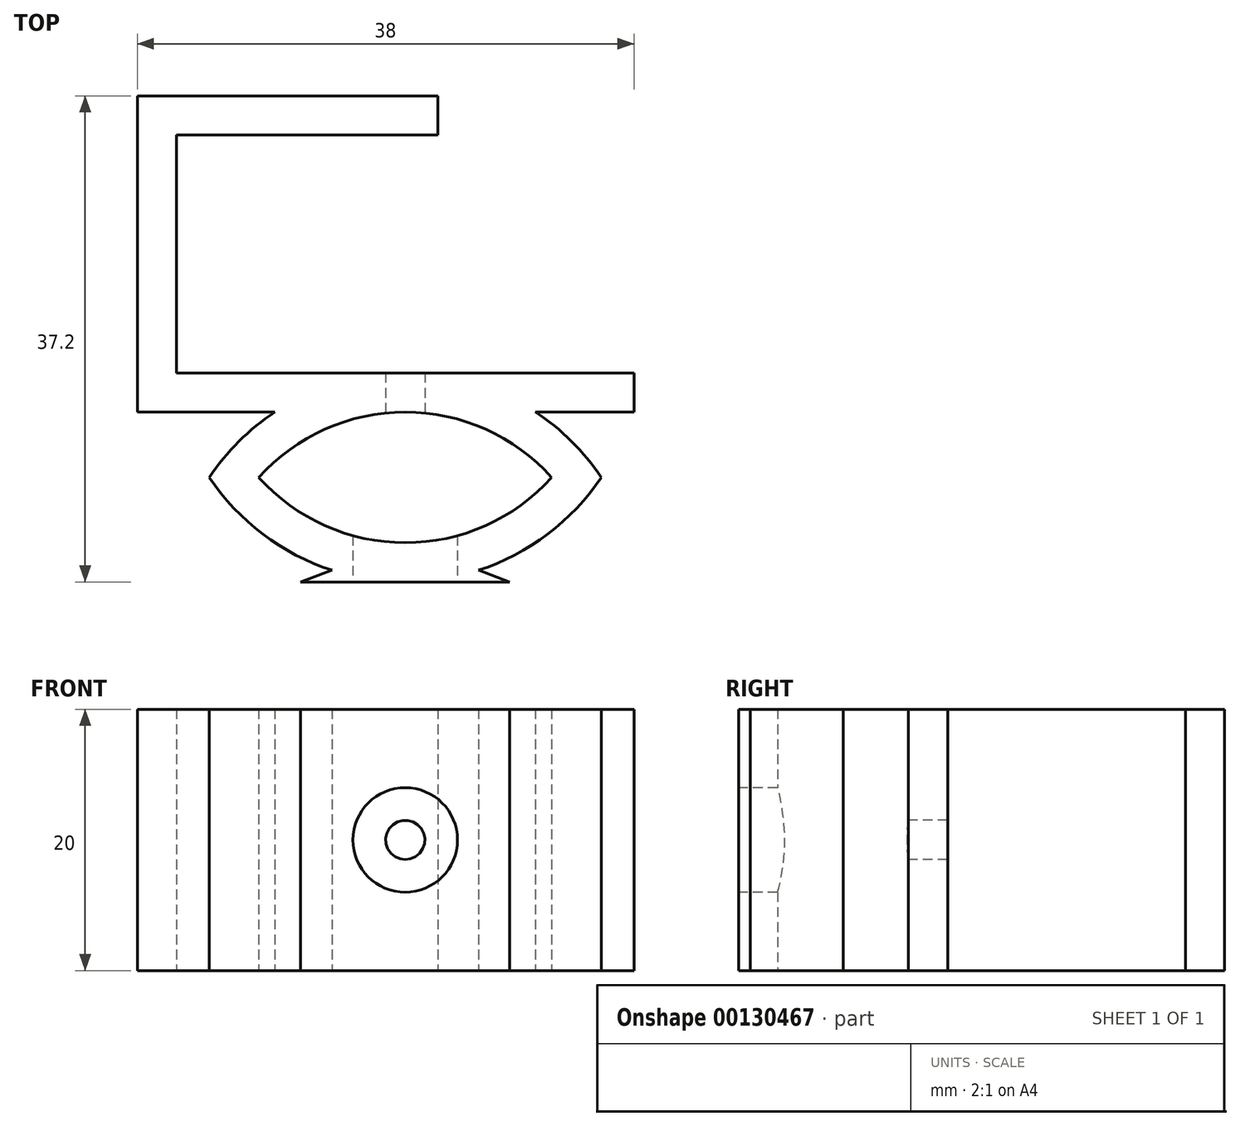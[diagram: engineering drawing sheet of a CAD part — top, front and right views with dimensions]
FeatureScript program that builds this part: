
annotation { "Feature Type Name" : "Feature", "Feature Type Description" : "" }
export const myFeature = defineFeature(function(context is Context, id is Id, definition is map)
    precondition{}
    {
        {
            var Q0;
            Q0=qCreatedBy(makeId("Top.planeOp"),FACE);
            var sketch = newSketch(context, id + "F0", { "sketchPlane" : qUnion([Q0])});
            skLineSegment(sketch, "E0", {"start": v(0, 0) * mm, "end": v(-20, 0) * mm});
            skLineSegment(sketch, "E1", {"start": v(-20, 0) * mm, "end": v(-20, -18.2) * mm});
            skLineSegment(sketch, "E2", {"start": v(-20, -18.2) * mm, "end": v(15, -18.2) * mm});
            skLineSegment(sketch, "E3.0", {"start": v(-23, -21.2) * mm, "end": v(15, -21.2) * mm});
            skLineSegment(sketch, "E3.1", {"start": v(-23, 3) * mm, "end": v(-23, -21.2) * mm});
            skLineSegment(sketch, "E3.2", {"start": v(0, 3) * mm, "end": v(-23, 3) * mm});
            skLineSegment(sketch, "E4", {"start": v(0, 3) * mm, "end": v(0, 0) * mm});
            skLineSegment(sketch, "E5", {"start": v(15, -18.2) * mm, "end": v(15, -21.2) * mm});
            skLineSegment(sketch, "E6", {"start": v(-17.5, -26.2) * mm, "end": v(12.5, -26.2) * mm, "construction": true});
            skLineSegment(sketch, "E7", {"start": v(-2.5, -18.2) * mm, "end": v(-2.5, -26.2) * mm, "construction": true});
            skPoint(sketch, "E8", {"position": v(-2.5, -26.2) * mm});
            skLineSegment(sketch, "E9", {"start": v(-2.5, -26.2) * mm, "end": v(-2.5, -34.2) * mm, "construction": true});
            skArc(sketch, "E10", {"start": v(12.5, -26.2) * mm, "mid": v(-2.5, -18.2) * mm, "end": v(-17.5, -26.2) * mm});
            skArc(sketch, "E11", {"start": v(-17.5, -26.2) * mm, "mid": v(-2.5, -34.2) * mm, "end": v(12.5, -26.2) * mm});
            skArc(sketch, "E12.0", {"start": v(8.7, -26.2) * mm, "mid": v(-2.5, -21.2) * mm, "end": v(-13.7, -26.2) * mm});
            skArc(sketch, "E12.1", {"start": v(-13.7, -26.2) * mm, "mid": v(-2.5, -31.2) * mm, "end": v(8.7, -26.2) * mm});
            skLineSegment(sketch, "E13", {"start": v(-2.5, -31.2) * mm, "end": v(-10.5, -34.2) * mm});
            skLineSegment(sketch, "E14", {"start": v(-10.5, -34.2) * mm, "end": v(5.5, -34.2) * mm});
            skLineSegment(sketch, "E15", {"start": v(5.5, -34.2) * mm, "end": v(-2.5, -31.2) * mm});
            skSolve(sketch);
        }
        {
            var Q0;
            Q0=makeQuery(id+"F0.imprint","IMPRINT",FACE,{"disambiguationData":[TD([[makeQuery(id+"F0.imprint","IMPRINT",EDGE,{"derivedFrom":sQuery(id+"F0.wireOp",EDGE,"E0")}),-1.0]])]});
            var Q1;
            {var subQ0=sQuery(id+"F0.wireOp",EDGE,"E10");var subQ1=sQuery(id+"F0.wireOp",EDGE,"E3.0");var subQ2=makeQuery(id+"F0.imprint","INTERSECT",VERTEX,{"disambiguationData":[OD(0.0)],"derivedFrom":[subQ1,subQ0]});Q1=makeQuery(id+"F0.imprint","IMPRINT",FACE,{"disambiguationData":[TD([[makeQuery(id+"F0.imprint","IMPRINT",EDGE,{"disambiguationData":[TD([[subQ2,-1.0]])],"derivedFrom":subQ1}),1.0]])]});}
            var Q2;
            {var subQ0=sQuery(id+"F0.wireOp",EDGE,"E5");Q2=makeQuery(id+"F0.imprint","IMPRINT",FACE,{"disambiguationData":[TD([[makeQuery(id+"F0.imprint","IMPRINT",EDGE,{"derivedFrom":subQ0}),-1.0]])]});}
            var Q3;
            {var subQ1=sQuery(id+"F0.wireOp",EDGE,"E10");var subQ3=sQuery(id+"F0.wireOp",EDGE,"E3.0");var subQ4=makeQuery(id+"F0.imprint","INTERSECT",VERTEX,{"disambiguationData":[OD(1.0)],"derivedFrom":[subQ3,subQ1]});Q3=makeQuery(id+"F0.imprint","IMPRINT",FACE,{"disambiguationData":[TD([[makeQuery(id+"F0.imprint","IMPRINT",EDGE,{"disambiguationData":[TD([[subQ4,1.0]])],"derivedFrom":subQ3}),-1.0]])]});}
            var Q4;
            {var subQ0=sQuery(id+"F0.wireOp",EDGE,"E13");var subQ1=sQuery(id+"F0.wireOp",EDGE,"E11");var subQ2=makeQuery(id+"F0.imprint","INTERSECT",VERTEX,{"derivedFrom":[subQ1,subQ0]});Q4=makeQuery(id+"F0.imprint","IMPRINT",FACE,{"disambiguationData":[TD([[makeQuery(id+"F0.imprint","IMPRINT",EDGE,{"disambiguationData":[TD([[subQ2,-1.0]])],"derivedFrom":subQ1}),1.0]])]});}
            var Q5;
            {var subQ1=sQuery(id+"F0.wireOp",EDGE,"E10");var subQ5=sQuery(id+"F0.wireOp",EDGE,"E3.0");var subQ6=makeQuery(id+"F0.imprint","INTERSECT",VERTEX,{"disambiguationData":[OD(0.0)],"derivedFrom":[subQ5,subQ1]});Q5=makeQuery(id+"F0.imprint","IMPRINT",FACE,{"disambiguationData":[TD([[makeQuery(id+"F0.imprint","IMPRINT",EDGE,{"disambiguationData":[TD([[subQ6,-1.0]])],"derivedFrom":subQ5}),-1.0]])]});}
            var Q6;
            {var subQ0=sQuery(id+"F0.wireOp",EDGE,"E13");var subQ1=sQuery(id+"F0.wireOp",EDGE,"E11");var subQ2=makeQuery(id+"F0.imprint","INTERSECT",VERTEX,{"derivedFrom":[subQ1,subQ0]});Q6=makeQuery(id+"F0.imprint","IMPRINT",FACE,{"disambiguationData":[TD([[makeQuery(id+"F0.imprint","IMPRINT",EDGE,{"disambiguationData":[TD([[subQ2,-1.0]])],"derivedFrom":subQ1}),-1.0]])]});}
            var Q7;
            {var subQ0=sQuery(id+"F0.wireOp",EDGE,"E14");var subQ1=sQuery(id+"F0.wireOp",EDGE,"E11");var subQ2=makeQuery(id+"F0.imprint","INTERSECT",VERTEX,{"derivedFrom":[subQ1,subQ0]});Q7=makeQuery(id+"F0.imprint","IMPRINT",FACE,{"disambiguationData":[TD([[makeQuery(id+"F0.imprint","IMPRINT",EDGE,{"disambiguationData":[TD([[subQ2,-1.0]])],"derivedFrom":subQ1}),-1.0]])]});}
            extrude(context, id + "F1", {"entities" : qUnion([Q0, Q1, Q2, Q3, Q4, Q5, Q6, Q7]), "depth" : 20 * mm});
        }
        {
            var Q0;
            Q0=makeQuery(id+"F1.opExtrude","SWEPT_FACE",FACE,{"disambiguationData":[OSD([sQuery(id+"F0.wireOp",EDGE,"E14")])]});
            var sketch = newSketch(context, id + "F2", { "sketchPlane" : qUnion([Q0])});
            skCircle(sketch, "E16", {"center": v(-2.5, 10) * mm, "radius": 4 * mm});
            skPoint(sketch, "E16.centerSnap0", {"position": v(-10.5, 10) * mm});
            skPoint(sketch, "E16.centerSnap1", {"position": v(-2.5, 20) * mm});
            skCircle(sketch, "E17", {"center": v(-2.5, 10) * mm, "radius": 1.5 * mm});
            skSolve(sketch);
        }
        {
            var Q0;
            Q0 = qSketchRegion(id + "F2", true);
            extrude(context, id + "F3", {"entities" : qUnion([Q0]), "operationType" : NewBodyOperationType.REMOVE, "oppositeDirection" : true, "depth" : 4 * mm});
        }
        {
            var Q0;
            Q0=makeQuery(id+"F3.boolean.opBoolean","SPLIT",FACE,{"disambiguationData":[TD([makeQuery(id+"F3.opExtrude","SWEPT_FACE",FACE,{"disambiguationData":[OSD([sQuery(id+"F2.wireOp",EDGE,"E17")])]})])],"derivedFrom":makeQuery(id+"F1.opExtrude","SWEPT_FACE",FACE,{"disambiguationData":[OSD([sQuery(id+"F0.wireOp",EDGE,"E14")])]})});
            extrude(context, id + "F4", {"entities" : qUnion([Q0]), "operationType" : NewBodyOperationType.REMOVE, "oppositeDirection" : true, "depth" : 25 * mm});
        }
    });
